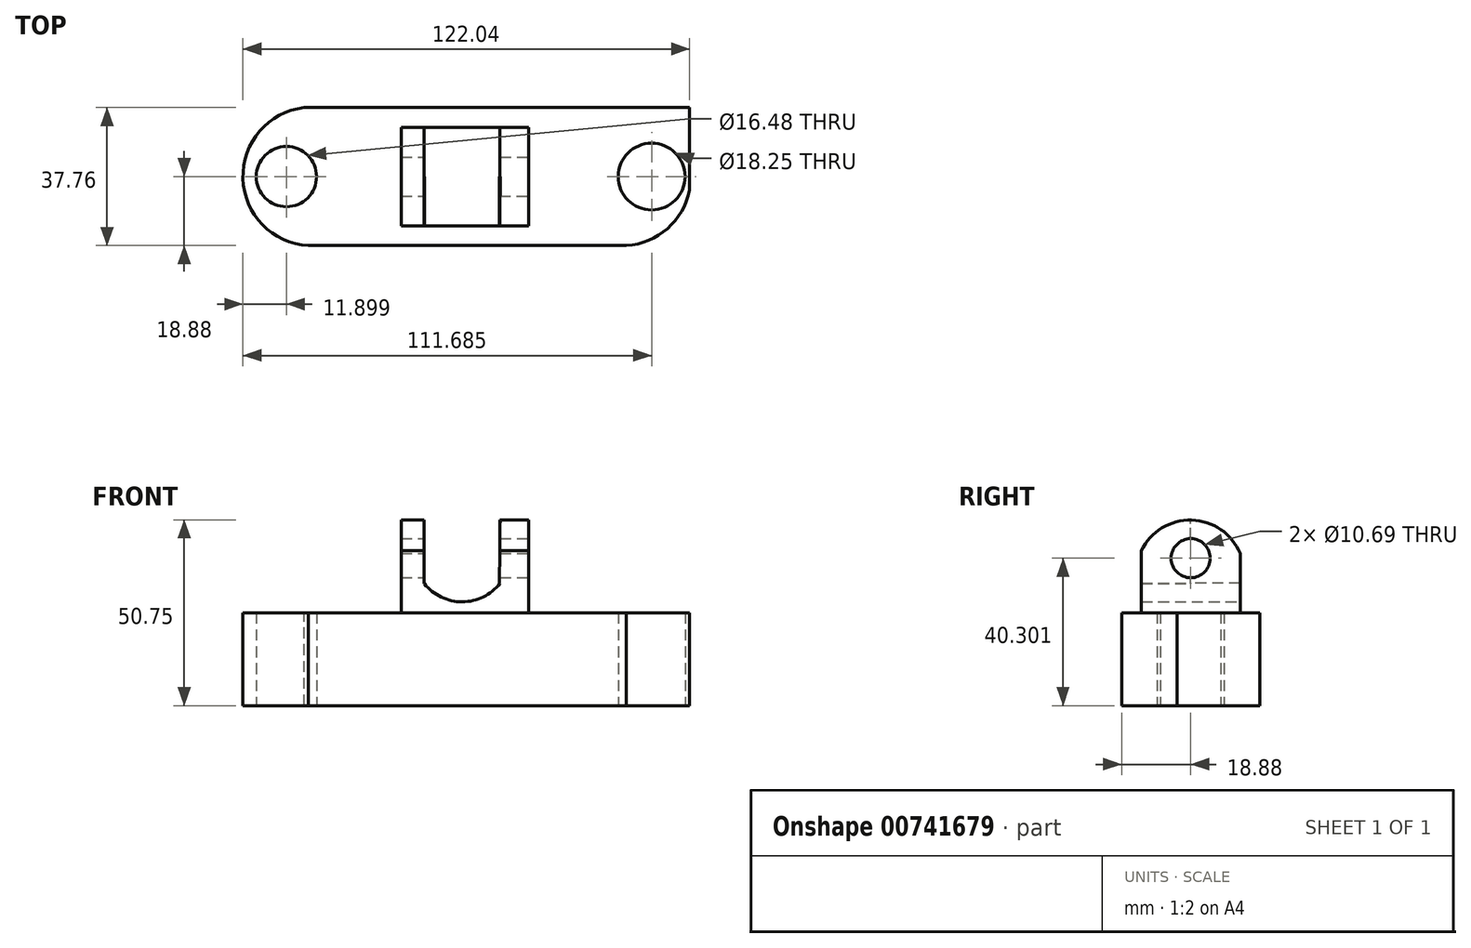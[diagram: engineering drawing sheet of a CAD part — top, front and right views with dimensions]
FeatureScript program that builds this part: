
annotation { "Feature Type Name" : "Feature", "Feature Type Description" : "" }
export const myFeature = defineFeature(function(context is Context, id is Id, definition is map)
    precondition{}
    {
        {
            var Q0;
            Q0=qCreatedBy(makeId("Top.planeOp"),FACE);
            var sketch = newSketch(context, id + "F0", { "sketchPlane" : qUnion([Q0])});
            skLineSegment(sketch, "E0.bottom", {"start": v(61.4, -18.88) * mm, "end": v(-61.4, -18.88) * mm});
            skLineSegment(sketch, "E0.top", {"start": v(61.4, 18.88) * mm, "end": v(-61.4, 18.88) * mm});
            skLineSegment(sketch, "E0.left", {"start": v(61.4, -18.88) * mm, "end": v(61.4, 18.88) * mm});
            skLineSegment(sketch, "E0.right", {"start": v(-61.4, -18.88) * mm, "end": v(-61.4, 18.88) * mm});
            skPoint(sketch, "E0.middle", {"position": v(0, 0) * mm});
            skSolve(sketch);
        }
        {
            var Q0;
            Q0=makeQuery(id+"F0.imprint","IMPRINT",FACE,{"disambiguationData":[TD([[makeQuery(id+"F0.imprint","IMPRINT",EDGE,{"derivedFrom":sQuery(id+"F0.wireOp",EDGE,"E0.bottom")}),-1.0]])]});
            extrude(context, id + "F1", {"entities" : qUnion([Q0]), "depth" : 25.4 * mm, "offsetDistance" : 25.4 * mm});
        }
        {
            var Q0;
            Q0=makeQuery(id+"F1.opExtrude","CAP_FACE",FACE,{"disambiguationData":[OSD([sQuery(id+"F0.wireOp",EDGE,"E0.bottom"),sQuery(id+"F0.wireOp",EDGE,"E0.top"),sQuery(id+"F0.wireOp",EDGE,"E0.left"),sQuery(id+"F0.wireOp",EDGE,"E0.right")])],"isStart":false});
            var sketch = newSketch(context, id + "F2", { "sketchPlane" : qUnion([Q0])});
            skArc(sketch, "E1", {"start": v(-39.4, 18.88) * mm, "mid": v(-60.62, 0.63) * mm, "end": v(-40.55, -18.88) * mm});
            skSolve(sketch);
        }
        {
            var Q0;
            {var subQ5=makeQuery(id+"F1.opExtrude","CAP_EDGE",EDGE,{"disambiguationData":[OSD([sQuery(id+"F0.wireOp",EDGE,"E0.right")])],"isStart":false});Q0=makeQuery(id+"F2.imprint","IMPRINT",FACE,{"disambiguationData":[TD([[makeQuery(id+"F2.imprint","IMPRINT",EDGE,{"derivedFrom":subQ5}),-1.0]])]});}
            extrude(context, id + "F3", {"entities" : qUnion([Q0]), "operationType" : NewBodyOperationType.REMOVE, "oppositeDirection" : true, "depth" : 25.4 * mm, "offsetDistance" : 25.4 * mm});
        }
        {
            var Q0;
            Q0=makeQuery(id+"F1.opExtrude","CAP_FACE",FACE,{"disambiguationData":[OSD([sQuery(id+"F0.wireOp",EDGE,"E0.bottom"),sQuery(id+"F0.wireOp",EDGE,"E0.top"),sQuery(id+"F0.wireOp",EDGE,"E0.left"),sQuery(id+"F0.wireOp",EDGE,"E0.right")])],"isStart":false});
            var sketch = newSketch(context, id + "F4", { "sketchPlane" : qUnion([Q0])});
            skArc(sketch, "E2", {"start": v(44.17, -18.88) * mm, "mid": v(61.75, 0.82) * mm, "end": v(42.49, 18.88) * mm});
            skSolve(sketch);
        }
        {
            var Q0;
            {var subQ0=sQuery(id+"F4.wireOp",EDGE,"E2");var subQ1=makeQuery(id+"F1.opExtrude","CAP_EDGE",EDGE,{"disambiguationData":[OSD([sQuery(id+"F0.wireOp",EDGE,"E0.bottom")])],"isStart":false});var subQ2=makeQuery(id+"F4.imprint","INTERSECT",VERTEX,{"derivedFrom":[subQ1,subQ0]});Q0=makeQuery(id+"F4.imprint","IMPRINT",FACE,{"disambiguationData":[TD([[makeQuery(id+"F4.imprint","IMPRINT",EDGE,{"disambiguationData":[TD([[subQ2,-1.0]])],"derivedFrom":subQ0}),-1.0]])]});}
            var Q1;
            {var subQ0=sQuery(id+"F4.wireOp",EDGE,"E2");var subQ1=makeQuery(id+"F1.opExtrude","CAP_EDGE",EDGE,{"disambiguationData":[OSD([sQuery(id+"F0.wireOp",EDGE,"E0.left")])],"isStart":false});var subQ2=makeQuery(id+"F4.imprint","INTERSECT",VERTEX,{"disambiguationData":[OD(1.0)],"derivedFrom":[subQ1,subQ0]});Q1=makeQuery(id+"F4.imprint","IMPRINT",FACE,{"disambiguationData":[TD([[makeQuery(id+"F4.imprint","IMPRINT",EDGE,{"disambiguationData":[TD([[subQ2,-1.0]])],"derivedFrom":subQ0}),-1.0]])]});}
            extrude(context, id + "F5", {"entities" : qUnion([Q0, Q1]), "operationType" : NewBodyOperationType.REMOVE, "oppositeDirection" : true, "depth" : 25.4 * mm, "offsetDistance" : 25.4 * mm});
        }
        {
            var Q0;
            Q0=qCreatedBy(makeId("Top.planeOp"),FACE);
            var sketch = newSketch(context, id + "F6", { "sketchPlane" : qUnion([Q0])});
            skCircle(sketch, "E3", {"center": v(-48.73, 0) * mm, "radius": 8.24 * mm});
            skSolve(sketch);
        }
        {
            var Q0;
            Q0=makeQuery(id+"F6.imprint","IMPRINT",FACE,{"disambiguationData":[TD([[makeQuery(id+"F6.imprint","IMPRINT",EDGE,{"derivedFrom":sQuery(id+"F6.wireOp",EDGE,"E3")}),1.0]])]});
            extrude(context, id + "F7", {"entities" : qUnion([Q0]), "operationType" : NewBodyOperationType.REMOVE, "depth" : 76.2 * mm, "offsetDistance" : 25.4 * mm});
        }
        {
            var Q0;
            Q0=qCreatedBy(makeId("Top.planeOp"),FACE);
            var sketch = newSketch(context, id + "F8", { "sketchPlane" : qUnion([Q0])});
            skCircle(sketch, "E4", {"center": v(51.06, 0) * mm, "radius": 9.12 * mm});
            skSolve(sketch);
        }
        {
            var Q0;
            Q0=makeQuery(id+"F8.imprint","IMPRINT",FACE,{"disambiguationData":[TD([[makeQuery(id+"F8.imprint","IMPRINT",EDGE,{"derivedFrom":sQuery(id+"F8.wireOp",EDGE,"E4")}),1.0]])]});
            extrude(context, id + "F9", {"entities" : qUnion([Q0]), "operationType" : NewBodyOperationType.REMOVE, "depth" : 25.4 * mm, "offsetDistance" : 25.4 * mm});
        }
        {
            var Q0;
            Q0=qCreatedBy(makeId("Top.planeOp"),FACE);
            var sketch = newSketch(context, id + "F10", { "sketchPlane" : qUnion([Q0])});
            skLineSegment(sketch, "E5.bottom", {"start": v(17.4, 13.5) * mm, "end": v(-17.4, 13.5) * mm});
            skLineSegment(sketch, "E5.top", {"start": v(17.4, -13.5) * mm, "end": v(-17.4, -13.5) * mm});
            skLineSegment(sketch, "E5.left", {"start": v(17.4, 13.5) * mm, "end": v(17.4, -13.5) * mm});
            skLineSegment(sketch, "E5.right", {"start": v(-17.4, 13.5) * mm, "end": v(-17.4, -13.5) * mm});
            skPoint(sketch, "E5.middle", {"position": v(0, 0) * mm});
            skSolve(sketch);
        }
        {
            var Q0;
            Q0=makeQuery(id+"F10.imprint","IMPRINT",FACE,{"disambiguationData":[TD([[makeQuery(id+"F10.imprint","IMPRINT",EDGE,{"derivedFrom":sQuery(id+"F10.wireOp",EDGE,"E5.bottom")}),1.0]])]});
            extrude(context, id + "F11", {"entities" : qUnion([Q0]), "operationType" : NewBodyOperationType.ADD, "depth" : 50.8 * mm, "offsetDistance" : 25.4 * mm});
        }
        {
            var Q0;
            Q0=makeQuery(id+"F11.opExtrude","SWEPT_FACE",FACE,{"disambiguationData":[OSD([sQuery(id+"F10.wireOp",EDGE,"E5.left")])]});
            var sketch = newSketch(context, id + "F12", { "sketchPlane" : qUnion([Q0])});
            skArc(sketch, "E6", {"start": v(13.5, 41.63) * mm, "mid": v(0.23, 50.74) * mm, "end": v(-13.5, 42.35) * mm});
            skSolve(sketch);
        }
        {
            var Q0;
            {var subQ0=sQuery(id+"F12.wireOp",EDGE,"E6");Q0=makeQuery(id+"F12.imprint","IMPRINT",FACE,{"disambiguationData":[TD([[makeQuery(id+"F12.imprint","IMPRINT",EDGE,{"derivedFrom":subQ0}),-1.0]])]});}
            extrude(context, id + "F13", {"entities" : qUnion([Q0]), "operationType" : NewBodyOperationType.REMOVE, "oppositeDirection" : true, "depth" : 25.4 * mm, "offsetDistance" : 25.4 * mm});
        }
        {
            var Q0;
            Q0=makeQuery(id+"F13.boolean.opBoolean","COPY",FACE,{"derivedFrom":makeQuery(id+"F13.opExtrude","CAP_FACE",FACE,{"disambiguationData":[OSD([sQuery(id+"F10.wireOp",EDGE,"E5.bottom"),sQuery(id+"F10.wireOp",EDGE,"E5.top"),sQuery(id+"F10.wireOp",EDGE,"E5.left"),sQuery(id+"F12.wireOp",EDGE,"E6")])],"isStart":false})});
            extrude(context, id + "F14", {"entities" : qUnion([Q0]), "operationType" : NewBodyOperationType.REMOVE, "oppositeDirection" : true, "depth" : 25.4 * mm, "offsetDistance" : 25.4 * mm});
        }
        {
            var Q0;
            Q0=qCreatedBy(makeId("Right.planeOp"),FACE);
            var sketch = newSketch(context, id + "F15", { "sketchPlane" : qUnion([Q0])});
            skCircle(sketch, "E7", {"center": v(0, 40.3) * mm, "radius": 5.34 * mm});
            skSolve(sketch);
        }
        {
            var Q0;
            Q0 = qSketchRegion(id + "F15", true);
            extrude(context, id + "F16", {"entities" : qUnion([Q0]), "operationType" : NewBodyOperationType.REMOVE, "oppositeDirection" : true, "depth" : 25.4 * mm, "offsetDistance" : 25.4 * mm});
        }
        {
            var Q0;
            Q0=makeQuery(id+"F16.boolean.opBoolean","COPY",FACE,{"derivedFrom":makeQuery(id+"F16.opExtrude","CAP_FACE",FACE,{"disambiguationData":[OSD([sQuery(id+"F15.wireOp",EDGE,"E7")])],"isStart":true})});
            extrude(context, id + "F17", {"entities" : qUnion([Q0]), "operationType" : NewBodyOperationType.REMOVE, "oppositeDirection" : true, "depth" : 25.4 * mm, "offsetDistance" : 25.4 * mm});
        }
        {
            var Q0;
            Q0=qCreatedBy(makeId("Front.planeOp"),FACE);
            var sketch = newSketch(context, id + "F18", { "sketchPlane" : qUnion([Q0])});
            skLineSegment(sketch, "E8", {"start": v(-11.11, 50.91) * mm, "end": v(-11.11, 33.42) * mm});
            skLineSegment(sketch, "E9", {"start": v(-11.11, 33.42) * mm, "end": v(9.63, 33.42) * mm});
            skLineSegment(sketch, "E10", {"start": v(9.63, 33.42) * mm, "end": v(9.63, 50.92) * mm});
            skLineSegment(sketch, "E11", {"start": v(9.63, 50.92) * mm, "end": v(-11.11, 50.91) * mm});
            skSolve(sketch);
        }
        {
            var Q0;
            Q0=qCreatedBy(makeId("Front.planeOp"),FACE);
            var sketch = newSketch(context, id + "F19", { "sketchPlane" : qUnion([Q0])});
            skLineSegment(sketch, "E12", {"start": v(9.64, 50.79) * mm, "end": v(-11.12, 50.79) * mm});
            skLineSegment(sketch, "E13", {"start": v(-11.12, 50.79) * mm, "end": v(-11.12, 33.34) * mm});
            skLineSegment(sketch, "E14", {"start": v(-11.12, 33.34) * mm, "end": v(9.46, 33.34) * mm});
            skLineSegment(sketch, "E15", {"start": v(9.46, 33.34) * mm, "end": v(9.64, 50.79) * mm});
            skSolve(sketch);
        }
        {
            var Q0;
            Q0 = qSketchRegion(id + "F19", true);
            extrude(context, id + "F20", {"entities" : qUnion([Q0]), "operationType" : NewBodyOperationType.REMOVE, "depth" : 50.8 * mm, "offsetDistance" : 25.4 * mm});
        }
        {
            var Q0;
            Q0=makeQuery(id+"F18.imprint","IMPRINT",FACE,{"disambiguationData":[TD([[makeQuery(id+"F18.imprint","IMPRINT",EDGE,{"derivedFrom":sQuery(id+"F18.wireOp",EDGE,"E8")}),1.0]])]});
            extrude(context, id + "F21", {"entities" : qUnion([Q0]), "operationType" : NewBodyOperationType.REMOVE, "oppositeDirection" : true, "depth" : 25.4 * mm, "offsetDistance" : 25.4 * mm});
        }
        {
            var Q0;
            Q0=makeQuery(id+"F11.opExtrude","SWEPT_FACE",FACE,{"disambiguationData":[OSD([sQuery(id+"F10.wireOp",EDGE,"E5.bottom")])]});
            var sketch = newSketch(context, id + "F22", { "sketchPlane" : qUnion([Q0])});
            skLineSegment(sketch, "E16", {"start": v(-9.63, 33.42) * mm, "end": v(11.11, 33.42) * mm});
            skArc(sketch, "E17", {"start": v(-9.63, 33.42) * mm, "mid": v(0.74, 28.38) * mm, "end": v(11.11, 33.42) * mm});
            skSolve(sketch);
        }
        {
            var Q0;
            Q0=makeQuery(id+"F22.imprint","IMPRINT",FACE,{"disambiguationData":[TD([[makeQuery(id+"F22.imprint","IMPRINT",EDGE,{"derivedFrom":sQuery(id+"F22.wireOp",EDGE,"E16")}),1.0]])]});
            extrude(context, id + "F23", {"entities" : qUnion([Q0]), "operationType" : NewBodyOperationType.REMOVE, "oppositeDirection" : true, "depth" : 50.8 * mm, "offsetDistance" : 25.4 * mm});
        }
    });
